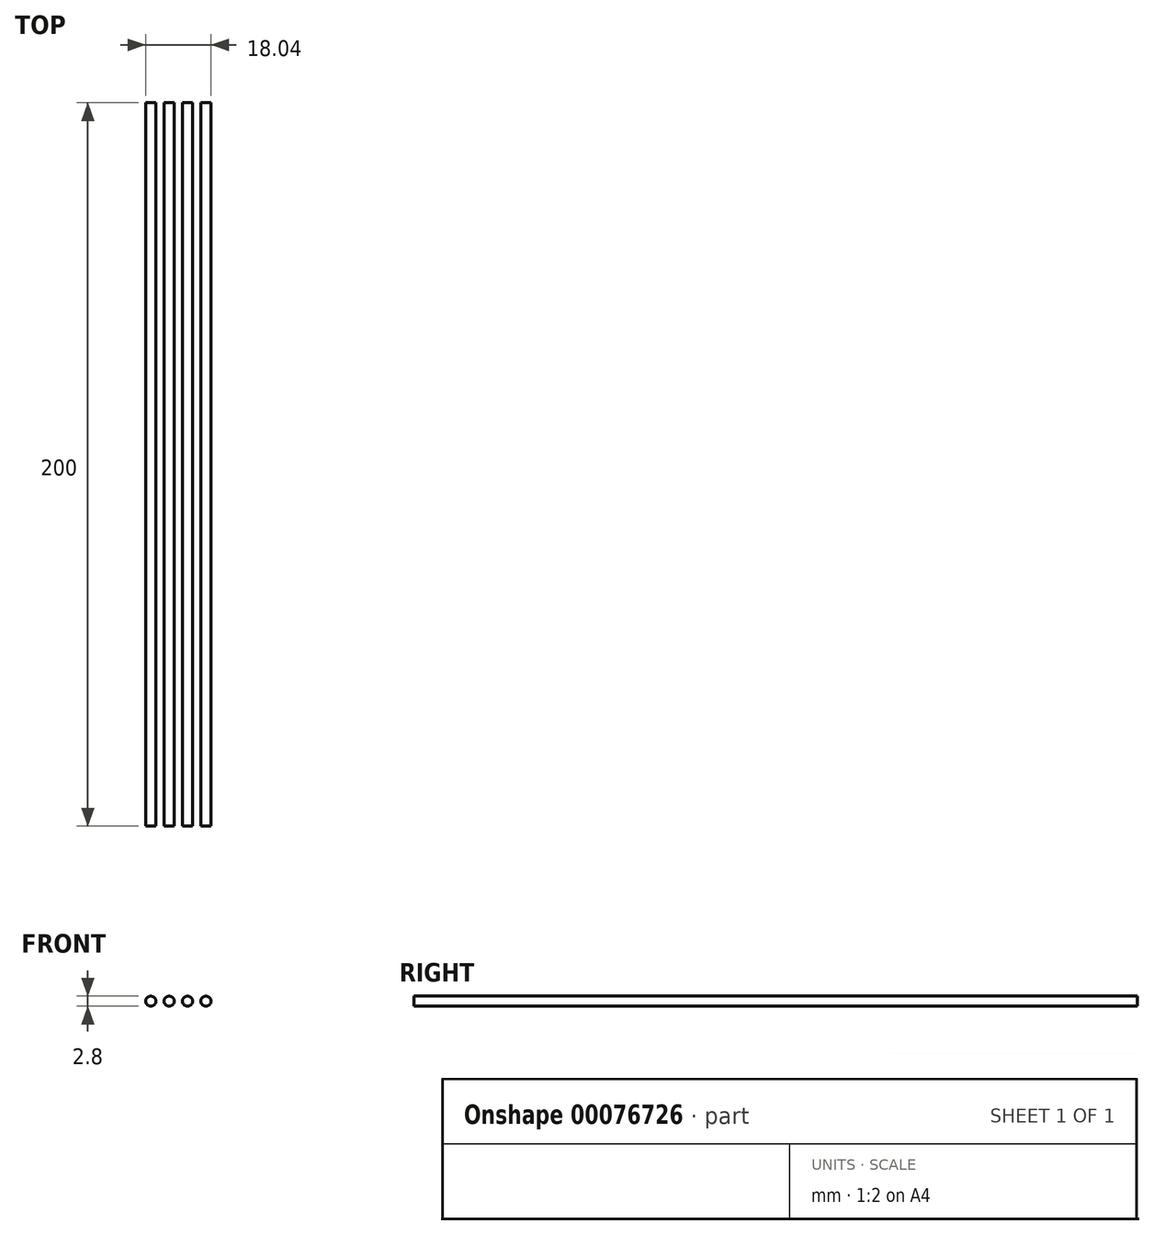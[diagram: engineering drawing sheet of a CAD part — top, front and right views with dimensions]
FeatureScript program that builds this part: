
annotation { "Feature Type Name" : "Feature", "Feature Type Description" : "" }
export const myFeature = defineFeature(function(context is Context, id is Id, definition is map)
    precondition{}
    {
        {
            var Q0;
            Q0=qCreatedBy(makeId("Front.planeOp"),FACE);
            var sketch = newSketch(context, id + "F0", { "sketchPlane" : qUnion([Q0])});
            skCircle(sketch, "E0", {"center": v(-7.62, 0) * mm, "radius": 1.4 * mm});
            skCircle(sketch, "E1.1.0.0", {"center": v(-2.54, 0) * mm, "radius": 1.4 * mm});
            skCircle(sketch, "E1.2.0.0", {"center": v(2.54, 0) * mm, "radius": 1.4 * mm});
            skCircle(sketch, "E1.3.0.0", {"center": v(7.62, 0) * mm, "radius": 1.4 * mm});
            skLineSegment(sketch, "E1.direction1", {"start": v(-7.62, 0) * mm, "end": v(-2.54, 0) * mm, "construction": true});
            skLineSegment(sketch, "E2", {"start": v(-2.54, 0) * mm, "end": v(2.54, 0) * mm, "construction": true});
            skLineSegment(sketch, "E3", {"start": v(2.54, 0) * mm, "end": v(7.62, 0) * mm, "construction": true});
            skSolve(sketch);
        }
        {
            var Q0;
            Q0 = qSketchRegion(id + "F0", true);
            extrude(context, id + "F1", {"entities" : qUnion([Q0]), "depth" : 200 * mm, "symmetric" : true});
        }
    });
